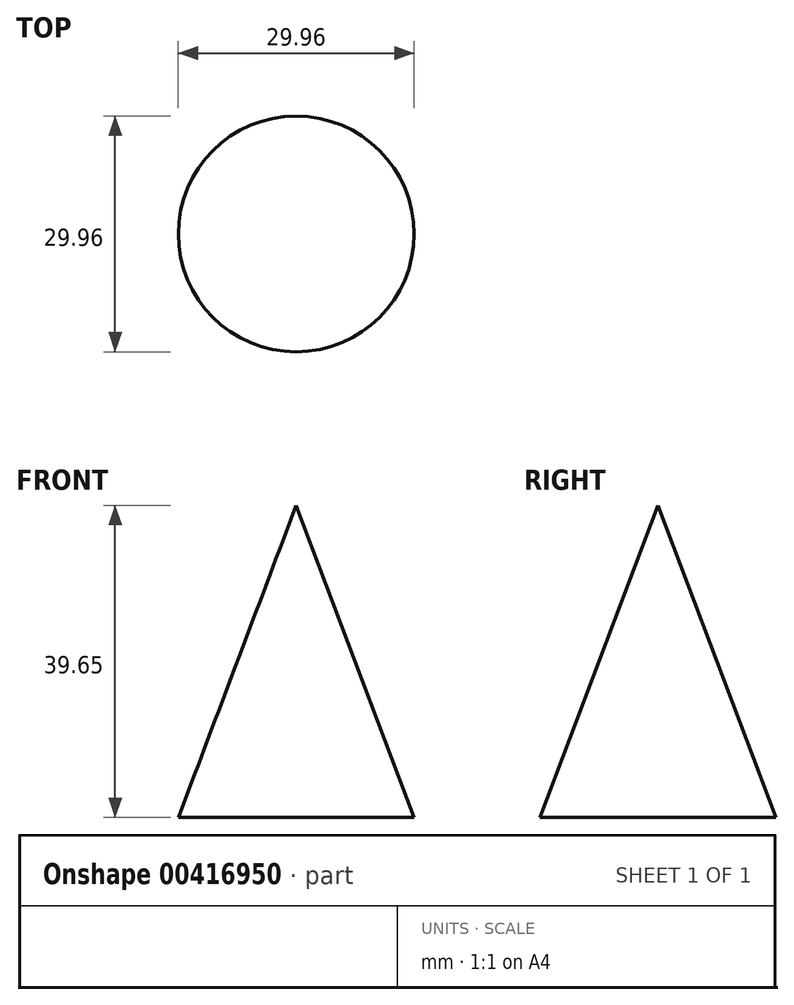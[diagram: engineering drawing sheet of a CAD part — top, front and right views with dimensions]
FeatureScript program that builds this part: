
annotation { "Feature Type Name" : "Feature", "Feature Type Description" : "" }
export const myFeature = defineFeature(function(context is Context, id is Id, definition is map)
    precondition{}
    {
        {
            var Q0;
            Q0=qCreatedBy(makeId("Front.planeOp"),FACE);
            var sketch = newSketch(context, id + "F0", { "sketchPlane" : qUnion([Q0])});
            skLineSegment(sketch, "E0", {"start": v(0, 0) * mm, "end": v(0, 39.65) * mm});
            skLineSegment(sketch, "E1", {"start": v(0, 39.65) * mm, "end": v(14.98, 0) * mm});
            skLineSegment(sketch, "E2", {"start": v(14.98, 0) * mm, "end": v(0, 0) * mm});
            skSolve(sketch);
        }
        {
            var Q0;
            Q0=makeQuery(id+"F0.imprint","IMPRINT",FACE,{"disambiguationData":[TD([[makeQuery(id+"F0.imprint","IMPRINT",EDGE,{"derivedFrom":sQuery(id+"F0.wireOp",EDGE,"E0")}),-1.0]])]});
            var Q1;
            Q1=sQuery(id+"F0.wireOp",EDGE,"E0");
            revolve(context, id + "F1", {"entities" : qUnion([Q0]), "axis" : qUnion([Q1]), "revolveType" : RevolveType.FULL});
        }
    });
